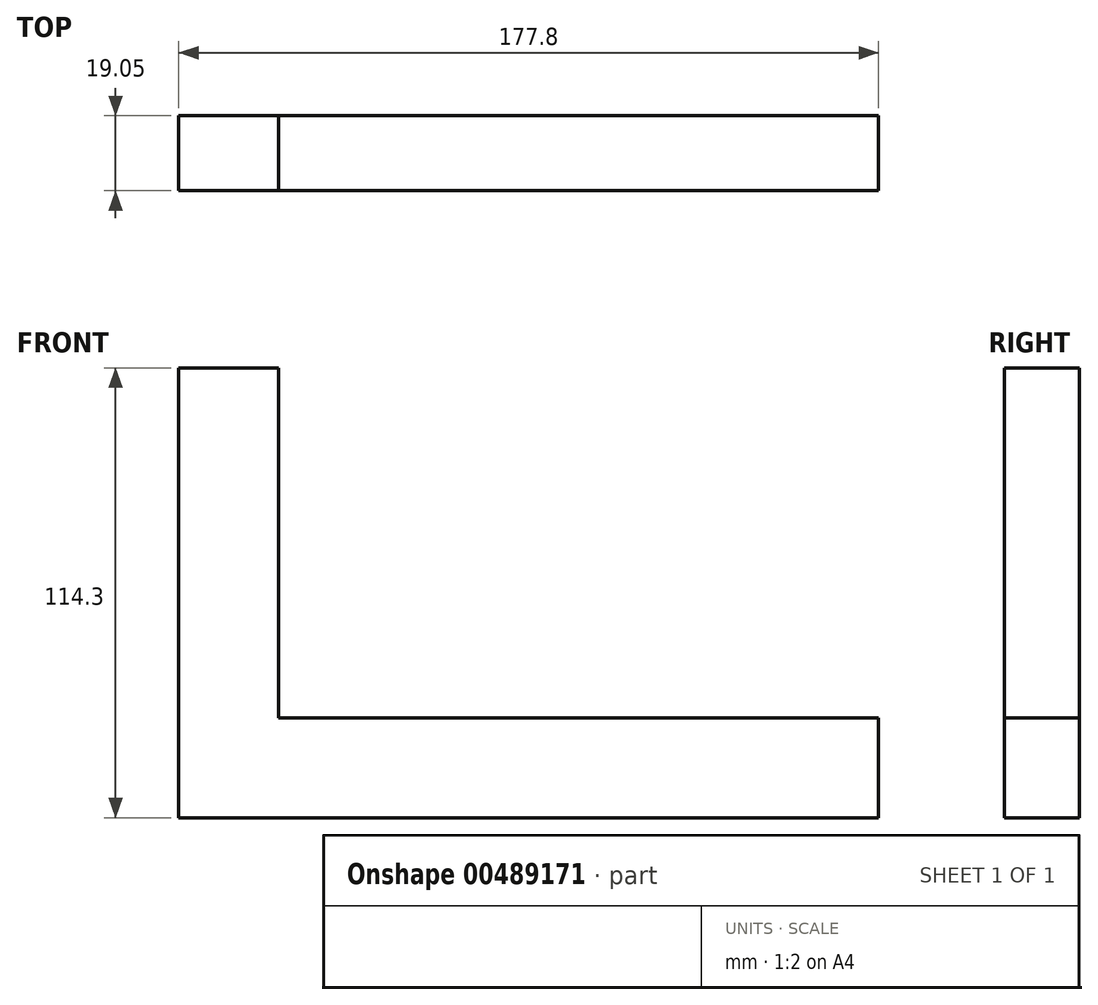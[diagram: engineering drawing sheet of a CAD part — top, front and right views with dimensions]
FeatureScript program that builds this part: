
annotation { "Feature Type Name" : "Feature", "Feature Type Description" : "" }
export const myFeature = defineFeature(function(context is Context, id is Id, definition is map)
    precondition{}
    {
        {
            var Q0;
            Q0=qCreatedBy(makeId("Front.planeOp"),FACE);
            var sketch = newSketch(context, id + "F0", { "sketchPlane" : qUnion([Q0])});
            skLineSegment(sketch, "E0", {"start": v(0, 0) * mm, "end": v(152.4, 0) * mm});
            skLineSegment(sketch, "E1", {"start": v(0, 0) * mm, "end": v(0, 88.9) * mm});
            skLineSegment(sketch, "E2", {"start": v(0, 88.9) * mm, "end": v(-25.4, 88.9) * mm});
            skLineSegment(sketch, "E3", {"start": v(152.4, 0) * mm, "end": v(152.4, -25.4) * mm});
            skLineSegment(sketch, "E4", {"start": v(-25.4, 88.9) * mm, "end": v(-25.4, -25.4) * mm});
            skLineSegment(sketch, "E5", {"start": v(-25.4, -25.4) * mm, "end": v(152.4, -25.4) * mm});
            skSolve(sketch);
        }
        {
            var Q0;
            Q0=makeQuery(id+"F0.imprint","IMPRINT",FACE,{"disambiguationData":[TD([[makeQuery(id+"F0.imprint","IMPRINT",EDGE,{"derivedFrom":sQuery(id+"F0.wireOp",EDGE,"E0")}),-1.0]])]});
            extrude(context, id + "F1", {"entities" : qUnion([Q0]), "depth" : 19.05 * mm, "offsetDistance" : 25.4 * mm});
        }
    });
